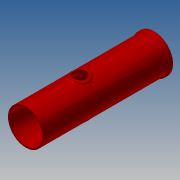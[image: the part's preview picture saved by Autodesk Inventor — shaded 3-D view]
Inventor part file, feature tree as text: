
AUTODESK INVENTOR PART (.ipt)
format: ipt  version: 2017.3 (Build 213257000, 257)  size: 312,320 bytes
history: native  units: in
note: dims shown in document units (in); Inventor stores cm internally (conversion verified against a paired STEP export)
features: other x3, extrude x3, sketch x3, pattern_circular x1, projected_geometry x1
ambient origin geometry x8: Origin, YZ Plane, XZ Plane, XY Plane, X Axis, Y Axis, Z Axis, Center Point
bodies: Solid1 (feature_tree)
feature tree (11):
  other  "A1-19027-400-07 HCWI liner - trunk.ipt"
  extrude  "Extrusion1"  Depth=0.5in TaperAngle=0.0deg
  extrude  "Extrusion2"  Depth=0.5in TaperAngle=0.0deg
  extrude  "Extrusion3"  [1 undecoded]
  pattern_circular  "Circular Pattern1"  [2 undecoded]
  other  "Solid1::A1-19027-400-07 HCWI liner - trunk.ipt"
  other  "TaggingFeature1"
  sketch  "Sketch2"  dims[d0=0.3937in d1=0.5in d2=1.0in d3=0.0in d4=0.0in]
  sketch  "Sketch3"  dims[d5=0.5in d6=0.5in d7=0.0in d8=0.0in d9=0.5in d10=0.0in]
  sketch  "Sketch4"  dims[d11=0.7874in d12=360.0deg]
  projected_geometry  "Projected Loop1"
note: 3 required parameter values undecoded (feature->parameter linkage not recoverable at this tier; creation-order binding heuristic only, values carry confidence <= 0.55)
